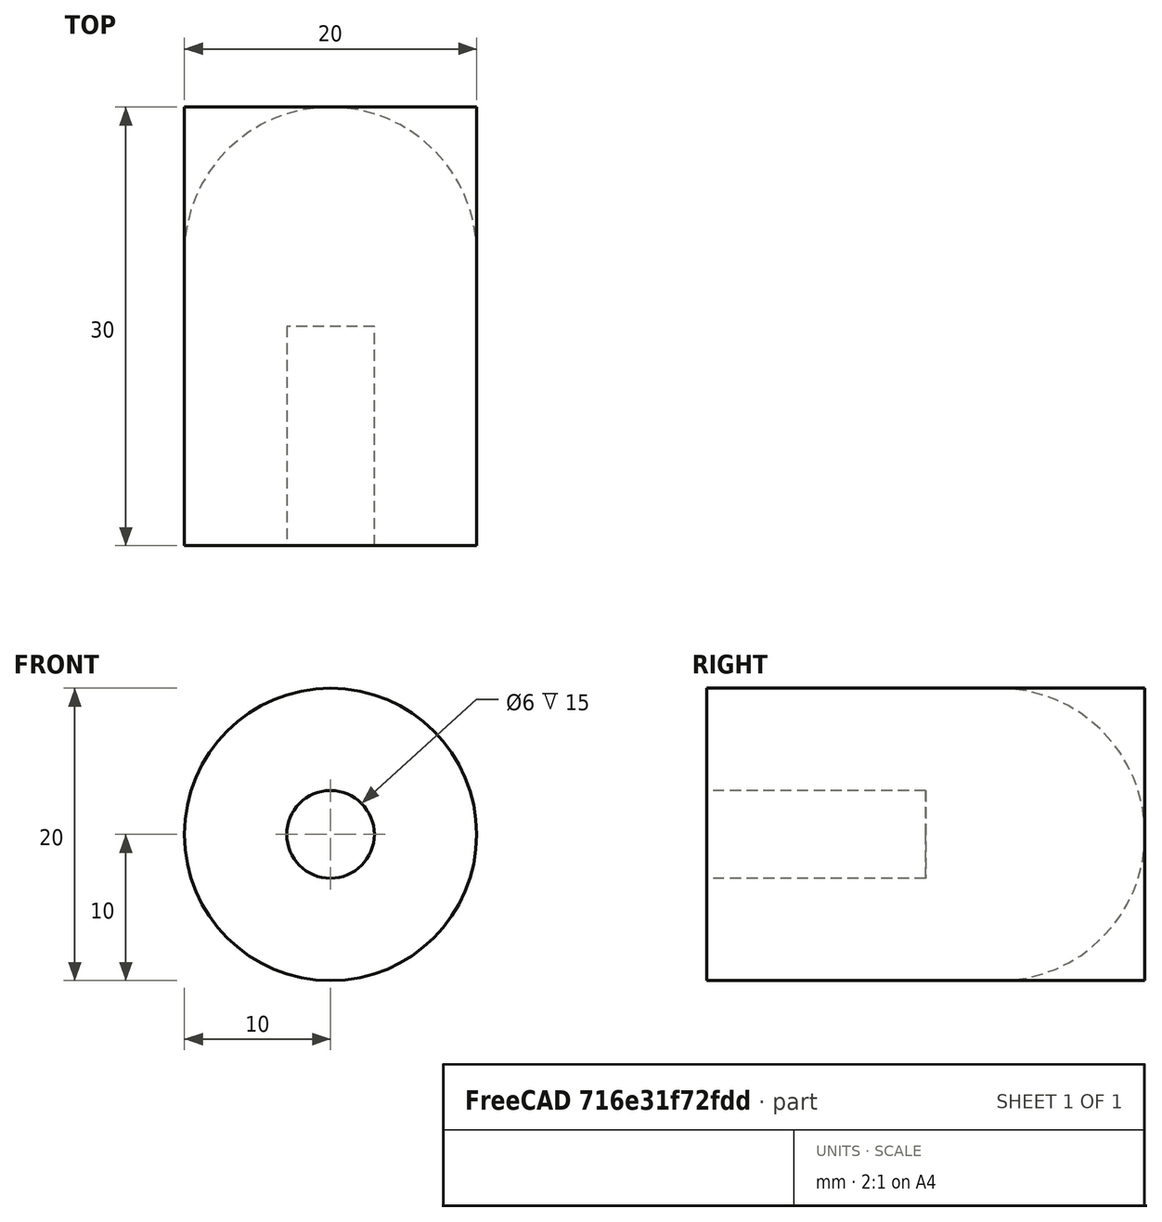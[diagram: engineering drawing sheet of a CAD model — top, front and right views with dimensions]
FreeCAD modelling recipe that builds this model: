
FCSTD DOCUMENT  (FreeCAD 0.15R4671 (Git))
Label: pendulum-bob
License: All rights reserved
LicenseURL: http://en.wikipedia.org/wiki/All_rights_reserved
objects: Sketcher::SketchObject×2, PartDesign::Pad×1, PartDesign::Pocket×1, PartDesign::Fillet×1, Mesh::Feature×1
note: 7 computed .brp shape members not serialized (recipe doc carries the construction recipe); baked Part::Feature solids carry a one-line shape summary decoded from their .brp

FEATURE [Sketcher::SketchObject] Sketch
  Placement = pos=(0,0,0) rot=(-1,0,0;4.71239rad)
  sketch-geometry (1):
    g0: Circle CenterX=0 CenterY=0 CenterZ=0 NormalX=0 NormalY=0 NormalZ=1 Radius=10
  constraints (3):
    c: DistanceY(g0) = 0
    c: DistanceX(g0) = 0
    c: Radius(g0) = 10
FEATURE [PartDesign::Pad] Pad
  Length = 30
  Length2 = 100
  Placement = pos=(0,0,0) rot=(-1,0,0;4.71239rad)
  Reversed = true
  Sketch = -> Sketch
  Type = 0
FEATURE [Sketcher::SketchObject] Sketch001
  Placement = pos=(0,0,0) rot=(1,0,0;1.5708rad)
  Support = -> Pad [Face2]
  sketch-geometry (1):
    g0: Circle CenterX=0 CenterY=0 CenterZ=0 NormalX=0 NormalY=0 NormalZ=1 Radius=3
  constraints (3):
    c: DistanceY(g0) = 0
    c: DistanceX(g0) = 0
    c: Radius(g0) = 3
FEATURE [PartDesign::Pocket] Pocket
  Length = 15
  Placement = pos=(0,0,0) rot=(-1,0,0;4.71239rad)
  Sketch = -> Sketch001
  Type = 0
FEATURE [PartDesign::Fillet] Fillet
  Base = -> Pocket [Edge3]
  Placement = pos=(0,0,0) rot=(-1,0,0;4.71239rad)
  Radius = 10
FEATURE [Mesh::Feature] Mesh  label="Fillet (Meshed)"
